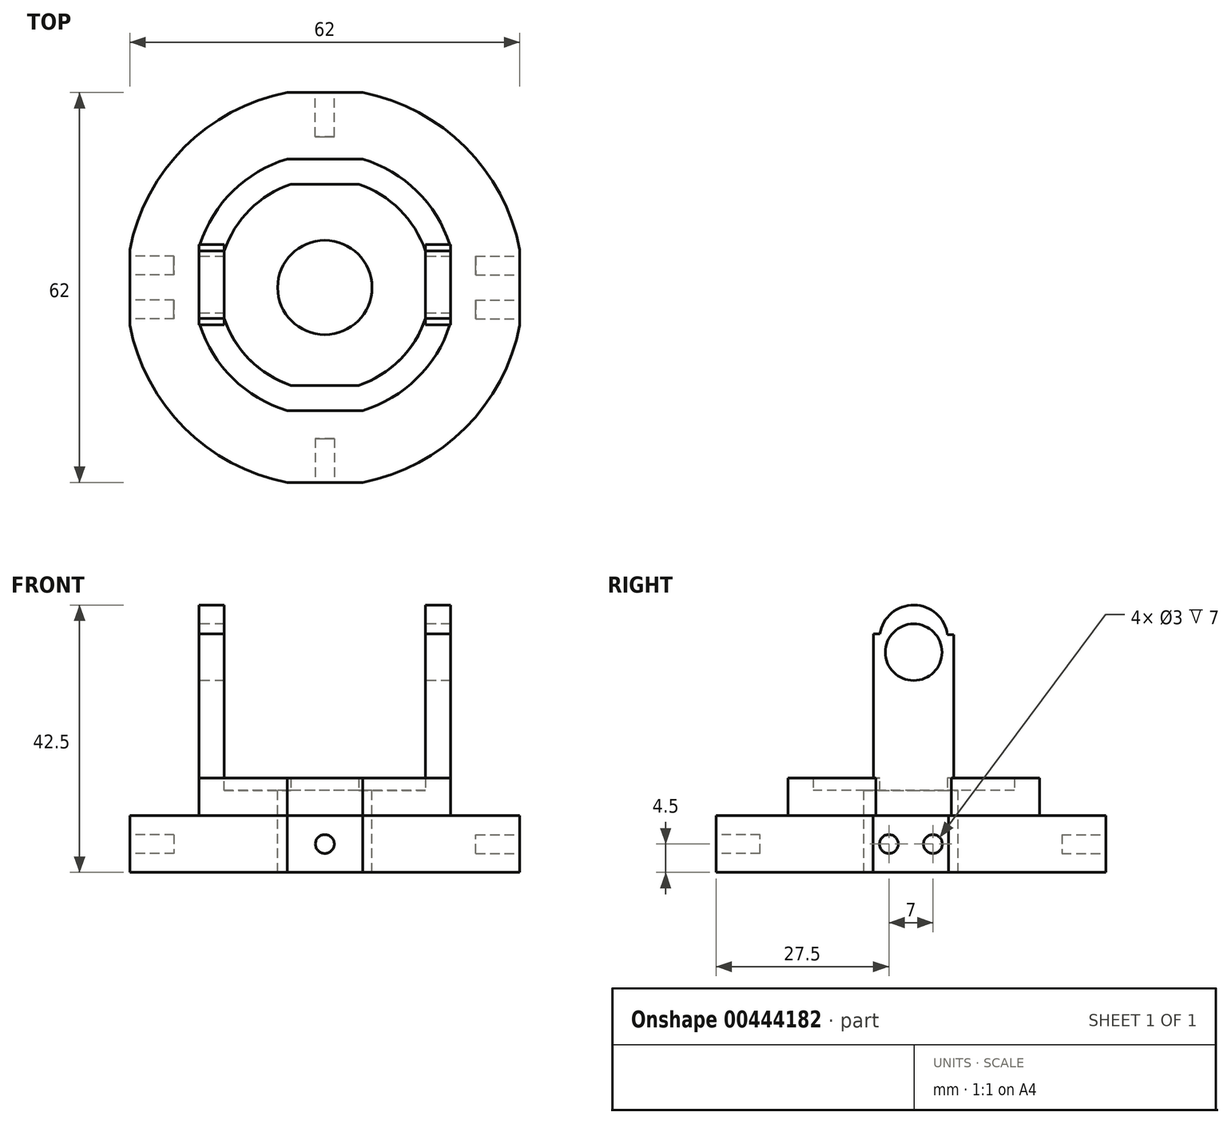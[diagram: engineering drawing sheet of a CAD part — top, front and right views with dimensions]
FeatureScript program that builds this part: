
annotation { "Feature Type Name" : "Feature", "Feature Type Description" : "" }
export const myFeature = defineFeature(function(context is Context, id is Id, definition is map)
    precondition{}
    {
        {
            var Q0;
            Q0=qCreatedBy(makeId("Top.planeOp"),FACE);
            var sketch = newSketch(context, id + "F0", { "sketchPlane" : qUnion([Q0])});
            skLineSegment(sketch, "E0", {"start": v(0, 20.44) * mm, "end": v(6, 20.44) * mm});
            skLineSegment(sketch, "E1", {"start": v(0, 20.44) * mm, "end": v(-6, 20.44) * mm});
            skLineSegment(sketch, "E2", {"start": v(20, 6.44) * mm, "end": v(20, -5.56) * mm});
            skLineSegment(sketch, "E3", {"start": v(0, -19.56) * mm, "end": v(6, -19.56) * mm});
            skLineSegment(sketch, "E4", {"start": v(0, -19.56) * mm, "end": v(-6, -19.56) * mm});
            skLineSegment(sketch, "E5", {"start": v(-20, 0.44) * mm, "end": v(-20, 6.44) * mm});
            skLineSegment(sketch, "E6", {"start": v(-20, 0.44) * mm, "end": v(-20, -5.56) * mm});
            skArc(sketch, "E7", {"start": v(-6, 20.44) * mm, "mid": v(-14.76, 15.2) * mm, "end": v(-20, 6.44) * mm});
            skArc(sketch, "E8.trimOffspring", {"start": v(20, 6.44) * mm, "mid": v(14.76, 15.2) * mm, "end": v(6, 20.44) * mm});
            skArc(sketch, "E9.trimOffspring", {"start": v(-20, -5.56) * mm, "mid": v(-14.76, -14.33) * mm, "end": v(-6, -19.56) * mm});
            skArc(sketch, "E10.trimOffspring", {"start": v(6, -19.56) * mm, "mid": v(14.76, -14.33) * mm, "end": v(20, -5.56) * mm});
            skSolve(sketch);
        }
        {
            var Q0;
            Q0=makeQuery(id+"F0.imprint","IMPRINT",FACE,{"disambiguationData":[TD([[makeQuery(id+"F0.imprint","IMPRINT",EDGE,{"derivedFrom":sQuery(id+"F0.wireOp",EDGE,"E0")}),-1.0]])]});
            extrude(context, id + "F1", {"entities" : qUnion([Q0]), "depth" : 6 * mm});
        }
        {
            var Q0;
            Q0=makeQuery(id+"F1.opExtrude","CAP_FACE",FACE,{"disambiguationData":[OSD([sQuery(id+"F0.wireOp",EDGE,"E0"),sQuery(id+"F0.wireOp",EDGE,"E1"),sQuery(id+"F0.wireOp",EDGE,"E2"),sQuery(id+"F0.wireOp",EDGE,"E3"),sQuery(id+"F0.wireOp",EDGE,"E4"),sQuery(id+"F0.wireOp",EDGE,"E5"),sQuery(id+"F0.wireOp",EDGE,"E6"),sQuery(id+"F0.wireOp",EDGE,"E7"),sQuery(id+"F0.wireOp",EDGE,"E8.trimOffspring"),sQuery(id+"F0.wireOp",EDGE,"E9.trimOffspring"),sQuery(id+"F0.wireOp",EDGE,"E10.trimOffspring")])],"isStart":false});
            shell(context, id + "F2", {"entities" : qUnion([Q0]), "thickness" : 4 * mm});
        }
        {
            var Q0;
            Q0=makeQuery(id+"F2.opShell","OFFSET_FACE",FACE,{"disambiguationData":[OSD([sQuery(id+"F0.wireOp",EDGE,"E0"),sQuery(id+"F0.wireOp",EDGE,"E1"),sQuery(id+"F0.wireOp",EDGE,"E2"),sQuery(id+"F0.wireOp",EDGE,"E3"),sQuery(id+"F0.wireOp",EDGE,"E4"),sQuery(id+"F0.wireOp",EDGE,"E5"),sQuery(id+"F0.wireOp",EDGE,"E6"),sQuery(id+"F0.wireOp",EDGE,"E7"),sQuery(id+"F0.wireOp",EDGE,"E8.trimOffspring"),sQuery(id+"F0.wireOp",EDGE,"E9.trimOffspring"),sQuery(id+"F0.wireOp",EDGE,"E10.trimOffspring")])]});
            extrude(context, id + "F3", {"entities" : qUnion([Q0]), "operationType" : NewBodyOperationType.REMOVE, "oppositeDirection" : true, "depth" : 25.4 * mm});
        }
        {
            var Q0;
            {var subQ0=sQuery(id+"F0.wireOp",EDGE,"E2");Q0=makeQuery(id+"F3.boolean.opBoolean","MERGE",FACE,{"derivedFrom":[makeQuery(id+"F2.opShell","OFFSET_FACE",FACE,{"disambiguationData":[OSD([subQ0])]}),makeQuery(id+"F3.opExtrude","SWEPT_FACE",FACE,{"disambiguationData":[OSD([subQ0])]})]});}
            var sketch = newSketch(context, id + "F4", { "sketchPlane" : qUnion([Q0])});
            skLineSegment(sketch, "E11.bottom", {"start": v(4.94, 6) * mm, "end": v(-5.82, 6) * mm});
            skLineSegment(sketch, "E11.top", {"start": v(4.94, 33.5) * mm, "end": v(-5.82, 33.5) * mm});
            skLineSegment(sketch, "E11.left", {"start": v(4.94, 6) * mm, "end": v(4.94, 33.5) * mm});
            skLineSegment(sketch, "E11.right", {"start": v(-5.82, 6) * mm, "end": v(-5.82, 33.5) * mm});
            skSolve(sketch);
        }
        {
            var Q0;
            Q0=makeQuery(id+"F4.imprint","IMPRINT",FACE,{"disambiguationData":[TD([[makeQuery(id+"F4.imprint","IMPRINT",EDGE,{"derivedFrom":sQuery(id+"F4.wireOp",EDGE,"E11.bottom")}),1.0]])]});
            extrude(context, id + "F5", {"entities" : qUnion([Q0]), "operationType" : NewBodyOperationType.ADD, "oppositeDirection" : true, "depth" : 4 * mm});
        }
        {
            var Q0;
            {var subQ0=sQuery(id+"F0.wireOp",EDGE,"E6");var subQ1=sQuery(id+"F0.wireOp",EDGE,"E5");Q0=makeQuery(id+"F3.boolean.opBoolean","MERGE",FACE,{"derivedFrom":[makeQuery(id+"F2.opShell","OFFSET_FACE",FACE,{"disambiguationData":[OSD([subQ1,subQ0])]}),makeQuery(id+"F3.opExtrude","SWEPT_FACE",FACE,{"disambiguationData":[OSD([subQ1,subQ0])]})]});}
            var sketch = newSketch(context, id + "F6", { "sketchPlane" : qUnion([Q0])});
            skLineSegment(sketch, "E12.bottom", {"start": v(5.82, 6) * mm, "end": v(-4.94, 6) * mm});
            skLineSegment(sketch, "E12.top", {"start": v(5.82, 33.5) * mm, "end": v(-4.94, 33.5) * mm});
            skLineSegment(sketch, "E12.left", {"start": v(5.82, 6) * mm, "end": v(5.82, 33.5) * mm});
            skLineSegment(sketch, "E12.right", {"start": v(-4.94, 6) * mm, "end": v(-4.94, 33.5) * mm});
            skSolve(sketch);
        }
        {
            var Q0;
            Q0=makeQuery(id+"F6.imprint","IMPRINT",FACE,{"disambiguationData":[TD([[makeQuery(id+"F6.imprint","IMPRINT",EDGE,{"derivedFrom":sQuery(id+"F6.wireOp",EDGE,"E12.bottom")}),1.0]])]});
            extrude(context, id + "F7", {"entities" : qUnion([Q0]), "operationType" : NewBodyOperationType.ADD, "oppositeDirection" : true, "depth" : 4 * mm});
        }
        {
            var Q0;
            Q0=makeQuery(id+"F7.boolean.opBoolean","MERGE",FACE,{"derivedFrom":[makeQuery(id+"F1.opExtrude","SWEPT_FACE",FACE,{"disambiguationData":[OSD([sQuery(id+"F0.wireOp",EDGE,"E5"),sQuery(id+"F0.wireOp",EDGE,"E6")])]}),makeQuery(id+"F7.opExtrude","CAP_FACE",FACE,{"disambiguationData":[OSD([sQuery(id+"F6.wireOp",EDGE,"E12.bottom"),sQuery(id+"F6.wireOp",EDGE,"E12.top"),sQuery(id+"F6.wireOp",EDGE,"E12.left"),sQuery(id+"F6.wireOp",EDGE,"E12.right")])],"isStart":false})]});
            var sketch = newSketch(context, id + "F8", { "sketchPlane" : qUnion([Q0])});
            skCircle(sketch, "E13", {"center": v(-0.44, 26) * mm, "radius": 4.5 * mm});
            skPoint(sketch, "E14.orphan", {"position": v(-0.44, 33.5) * mm});
            skLineSegment(sketch, "E15", {"start": v(-0.44, 33.5) * mm, "end": v(-0.44, 28.06) * mm, "construction": true});
            skArc(sketch, "E16", {"start": v(3.9, 24.77) * mm, "mid": v(-0.44, 33.5) * mm, "end": v(-4.76, 24.77) * mm});
            skSolve(sketch);
        }
        {
            var Q0;
            {var subQ0=sQuery(id+"F8.wireOp",EDGE,"E16");var subQ1=makeQuery(id+"F7.opExtrude","CAP_EDGE",EDGE,{"disambiguationData":[OSD([sQuery(id+"F6.wireOp",EDGE,"E12.top")])],"isStart":false});var subQ2=makeQuery(id+"F8.imprint","INTERSECT",VERTEX,{"derivedFrom":[subQ1,subQ0]});Q0=makeQuery(id+"F8.imprint","IMPRINT",FACE,{"disambiguationData":[TD([[makeQuery(id+"F8.imprint","IMPRINT",EDGE,{"disambiguationData":[TD([[subQ2,-1.0]])],"derivedFrom":subQ0}),-1.0]])]});}
            extrude(context, id + "F9", {"entities" : qUnion([Q0]), "operationType" : NewBodyOperationType.REMOVE, "oppositeDirection" : true, "depth" : 50 * mm});
        }
        {
            var Q0;
            {var subQ0=sQuery(id+"F8.wireOp",EDGE,"E16");var subQ1=makeQuery(id+"F7.opExtrude","CAP_EDGE",EDGE,{"disambiguationData":[OSD([sQuery(id+"F6.wireOp",EDGE,"E12.right")])],"isStart":false});var subQ2=makeQuery(id+"F8.imprint","INTERSECT",VERTEX,{"disambiguationData":[OD(1.0)],"derivedFrom":[subQ1,subQ0]});Q0=makeQuery(id+"F8.imprint","IMPRINT",FACE,{"disambiguationData":[TD([[makeQuery(id+"F8.imprint","IMPRINT",EDGE,{"disambiguationData":[TD([[subQ2,-1.0]])],"derivedFrom":subQ0}),-1.0]])]});}
            extrude(context, id + "F10", {"entities" : qUnion([Q0]), "operationType" : NewBodyOperationType.REMOVE, "oppositeDirection" : true, "depth" : 50 * mm});
        }
        {
            var Q0;
            {var subQ0=sQuery(id+"F8.wireOp",EDGE,"E16");var subQ1=sQuery(id+"F8.wireOp",EDGE,"E13");var subQ2=makeQuery(id+"F8.imprint","INTERSECT",VERTEX,{"disambiguationData":[OD(0.0)],"derivedFrom":[subQ1,subQ0]});Q0=makeQuery(id+"F8.imprint","IMPRINT",FACE,{"disambiguationData":[TD([[makeQuery(id+"F8.imprint","IMPRINT",EDGE,{"disambiguationData":[TD([[subQ2,1.0]])],"derivedFrom":subQ1}),1.0]])]});}
            extrude(context, id + "F11", {"entities" : qUnion([Q0]), "operationType" : NewBodyOperationType.REMOVE, "oppositeDirection" : true, "depth" : 50 * mm});
        }
        {
            var Q0;
            Q0=makeQuery(id+"F7.opExtrude","SWEPT_FACE",FACE,{"disambiguationData":[OSD([sQuery(id+"F6.wireOp",EDGE,"E12.left")])]});
            extrude(context, id + "F12", {"entities" : qUnion([Q0]), "operationType" : NewBodyOperationType.ADD, "depth" : 1 * mm});
        }
        {
            var Q0;
            Q0=makeQuery(id+"F7.opExtrude","SWEPT_FACE",FACE,{"disambiguationData":[OSD([sQuery(id+"F6.wireOp",EDGE,"E12.right")])]});
            extrude(context, id + "F13", {"entities" : qUnion([Q0]), "operationType" : NewBodyOperationType.ADD, "depth" : 1 * mm});
        }
        {
            var Q0;
            Q0=makeQuery(id+"F5.opExtrude","SWEPT_FACE",FACE,{"disambiguationData":[OSD([sQuery(id+"F4.wireOp",EDGE,"E11.right")])]});
            extrude(context, id + "F14", {"entities" : qUnion([Q0]), "operationType" : NewBodyOperationType.ADD, "depth" : 1 * mm});
        }
        {
            var Q0;
            Q0=makeQuery(id+"F5.opExtrude","SWEPT_FACE",FACE,{"disambiguationData":[OSD([sQuery(id+"F4.wireOp",EDGE,"E11.left")])]});
            extrude(context, id + "F15", {"entities" : qUnion([Q0]), "operationType" : NewBodyOperationType.ADD, "depth" : 1 * mm});
        }
        {
            var Q0;
            Q0=qCreatedBy(makeId("Top.planeOp"),FACE);
            var sketch = newSketch(context, id + "F16", { "sketchPlane" : qUnion([Q0])});
            skLineSegment(sketch, "E17", {"start": v(-16.05, 0) * mm, "end": v(16.02, 0) * mm, "construction": true});
            skSolve(sketch);
        }
        {
            var Q0;
            Q0=makeQuery(id+"F1.opExtrude","CAP_FACE",FACE,{"disambiguationData":[OSD([sQuery(id+"F0.wireOp",EDGE,"E0"),sQuery(id+"F0.wireOp",EDGE,"E1"),sQuery(id+"F0.wireOp",EDGE,"E2"),sQuery(id+"F0.wireOp",EDGE,"E3"),sQuery(id+"F0.wireOp",EDGE,"E4"),sQuery(id+"F0.wireOp",EDGE,"E5"),sQuery(id+"F0.wireOp",EDGE,"E6"),sQuery(id+"F0.wireOp",EDGE,"E7"),sQuery(id+"F0.wireOp",EDGE,"E8.trimOffspring"),sQuery(id+"F0.wireOp",EDGE,"E9.trimOffspring"),sQuery(id+"F0.wireOp",EDGE,"E10.trimOffspring")])],"isStart":true});
            var sketch = newSketch(context, id + "F17", { "sketchPlane" : qUnion([Q0])});
            skLineSegment(sketch, "E18.bottom", {"start": v(-16, -0.44) * mm, "end": v(0, -0.44) * mm});
            skLineSegment(sketch, "E18.top", {"start": v(-16, 15.56) * mm, "end": v(0, 15.56) * mm});
            skLineSegment(sketch, "E18.left", {"start": v(-16, -0.44) * mm, "end": v(-16, 15.56) * mm});
            skLineSegment(sketch, "E18.right", {"start": v(0, -0.44) * mm, "end": v(0, 15.56) * mm});
            skLineSegment(sketch, "E19.bottom", {"start": v(16, -0.44) * mm, "end": v(0, -0.44) * mm});
            skLineSegment(sketch, "E19.top", {"start": v(16, 15.56) * mm, "end": v(0, 15.56) * mm});
            skLineSegment(sketch, "E19.left", {"start": v(16, -0.44) * mm, "end": v(16, 15.56) * mm});
            skLineSegment(sketch, "E20.top", {"start": v(-16, -16.44) * mm, "end": v(0, -16.44) * mm});
            skLineSegment(sketch, "E20.left", {"start": v(-16, -0.44) * mm, "end": v(-16, -16.44) * mm});
            skLineSegment(sketch, "E20.right", {"start": v(0, -0.44) * mm, "end": v(0, -16.44) * mm});
            skLineSegment(sketch, "E21.top", {"start": v(16, -16.44) * mm, "end": v(0, -16.44) * mm});
            skLineSegment(sketch, "E21.left", {"start": v(16, -0.44) * mm, "end": v(16, -16.44) * mm});
            skCircle(sketch, "E22", {"center": v(0, -0.44) * mm, "radius": 16.88 * mm});
            skSolve(sketch);
        }
        {
            var Q0;
            {var subQ0=sQuery(id+"F17.wireOp",EDGE,"E18.right");Q0=makeQuery(id+"F17.imprint","IMPRINT",FACE,{"disambiguationData":[TD([[makeQuery(id+"F17.imprint","IMPRINT",EDGE,{"derivedFrom":subQ0}),-1.0]])]});}
            var Q1;
            {var subQ4=sQuery(id+"F17.wireOp",EDGE,"E18.right");Q1=makeQuery(id+"F17.imprint","IMPRINT",FACE,{"disambiguationData":[TD([[makeQuery(id+"F17.imprint","IMPRINT",EDGE,{"derivedFrom":subQ4}),1.0]])]});}
            var Q2;
            {var subQ6=sQuery(id+"F17.wireOp",EDGE,"E18.bottom");Q2=makeQuery(id+"F17.imprint","IMPRINT",FACE,{"disambiguationData":[TD([[makeQuery(id+"F17.imprint","IMPRINT",EDGE,{"derivedFrom":subQ6}),-1.0]])]});}
            var Q3;
            {var subQ4=sQuery(id+"F17.wireOp",EDGE,"E19.bottom");Q3=makeQuery(id+"F17.imprint","IMPRINT",FACE,{"disambiguationData":[TD([[makeQuery(id+"F17.imprint","IMPRINT",EDGE,{"derivedFrom":subQ4}),1.0]])]});}
            extrude(context, id + "F18", {"entities" : qUnion([Q0, Q1, Q2, Q3]), "operationType" : NewBodyOperationType.ADD, "oppositeDirection" : true, "depth" : 4 * mm});
        }
        {
            var Q0;
            Q0=makeQuery(id+"F18.boolean.opBoolean","MERGE",FACE,{"derivedFrom":[makeQuery(id+"F1.opExtrude","CAP_FACE",FACE,{"disambiguationData":[OSD([sQuery(id+"F0.wireOp",EDGE,"E0"),sQuery(id+"F0.wireOp",EDGE,"E1"),sQuery(id+"F0.wireOp",EDGE,"E2"),sQuery(id+"F0.wireOp",EDGE,"E3"),sQuery(id+"F0.wireOp",EDGE,"E4"),sQuery(id+"F0.wireOp",EDGE,"E5"),sQuery(id+"F0.wireOp",EDGE,"E6"),sQuery(id+"F0.wireOp",EDGE,"E7"),sQuery(id+"F0.wireOp",EDGE,"E8.trimOffspring"),sQuery(id+"F0.wireOp",EDGE,"E9.trimOffspring"),sQuery(id+"F0.wireOp",EDGE,"E10.trimOffspring")])],"isStart":true}),makeQuery(id+"F18.opExtrude","CAP_FACE",FACE,{"disambiguationData":[OSD([sQuery(id+"F17.wireOp",EDGE,"E18.top"),sQuery(id+"F17.wireOp",EDGE,"E18.left"),sQuery(id+"F17.wireOp",EDGE,"E19.top"),sQuery(id+"F17.wireOp",EDGE,"E19.left"),sQuery(id+"F17.wireOp",EDGE,"E20.top"),sQuery(id+"F17.wireOp",EDGE,"E20.left"),sQuery(id+"F17.wireOp",EDGE,"E21.top"),sQuery(id+"F17.wireOp",EDGE,"E21.left"),sQuery(id+"F17.wireOp",EDGE,"E22")])],"isStart":true})]});
            var sketch = newSketch(context, id + "F19", { "sketchPlane" : qUnion([Q0])});
            skPoint(sketch, "E23.start.orphan", {"position": v(0, 0) * mm});
            skLineSegment(sketch, "E24.top", {"start": v(0, 31) * mm, "end": v(6, 31) * mm});
            skLineSegment(sketch, "E25.bottom", {"start": v(6, 31) * mm, "end": v(-6, 31) * mm});
            skLineSegment(sketch, "E25.top", {"start": v(6, -31) * mm, "end": v(-6, -31) * mm});
            skLineSegment(sketch, "E26.right", {"start": v(31, 0) * mm, "end": v(31, 6) * mm});
            skLineSegment(sketch, "E27.left", {"start": v(31, 6) * mm, "end": v(31, -6) * mm});
            skLineSegment(sketch, "E27.right", {"start": v(-31, 6) * mm, "end": v(-31, -6) * mm});
            skArc(sketch, "E28", {"start": v(6, -31) * mm, "mid": v(22.33, -22.33) * mm, "end": v(31, -6) * mm});
            skArc(sketch, "E29.trimOffspring", {"start": v(31, 6) * mm, "mid": v(22.33, 22.33) * mm, "end": v(6, 31) * mm});
            skArc(sketch, "E30.trimOffspring", {"start": v(-31, -6) * mm, "mid": v(-22.33, -22.33) * mm, "end": v(-6, -31) * mm});
            skArc(sketch, "E31.trimOffspring", {"start": v(-6, 31) * mm, "mid": v(-22.33, 22.33) * mm, "end": v(-31, 6) * mm});
            skPoint(sketch, "E24.bottom.end.orphan", {"position": v(6, 0) * mm});
            skPoint(sketch, "E26.top.start.orphan", {"position": v(0, 6) * mm});
            skSolve(sketch);
        }
        {
            var Q0;
            Q0 = qSketchRegion(id + "F19", true);
            extrude(context, id + "F20", {"entities" : qUnion([Q0]), "operationType" : NewBodyOperationType.ADD, "depth" : 9 * mm});
        }
        {
            var Q0;
            Q0=makeQuery(id+"F20.opExtrude","SWEPT_FACE",FACE,{"disambiguationData":[OSD([sQuery(id+"F19.wireOp",EDGE,"E25.bottom")])]});
            var sketch = newSketch(context, id + "F21", { "sketchPlane" : qUnion([Q0])});
            skLineSegment(sketch, "E32", {"start": v(0, 0) * mm, "end": v(0, -4.5) * mm, "construction": true});
            skCircle(sketch, "E33", {"center": v(0, -4.5) * mm, "radius": 1.5 * mm});
            skSolve(sketch);
        }
        {
            var Q0;
            Q0=makeQuery(id+"F21.imprint","IMPRINT",FACE,{"disambiguationData":[TD([[makeQuery(id+"F21.imprint","IMPRINT",EDGE,{"derivedFrom":sQuery(id+"F21.wireOp",EDGE,"E33")}),1.0]])]});
            extrude(context, id + "F22", {"entities" : qUnion([Q0]), "operationType" : NewBodyOperationType.REMOVE, "oppositeDirection" : true, "depth" : 7 * mm});
        }
        {
            var Q0;
            Q0=makeQuery(id+"F20.opExtrude","SWEPT_FACE",FACE,{"disambiguationData":[OSD([sQuery(id+"F19.wireOp",EDGE,"E25.top")])]});
            var sketch = newSketch(context, id + "F23", { "sketchPlane" : qUnion([Q0])});
            skLineSegment(sketch, "E34", {"start": v(0, 0) * mm, "end": v(0, -4.5) * mm, "construction": true});
            skCircle(sketch, "E35", {"center": v(0, -4.5) * mm, "radius": 1.5 * mm});
            skSolve(sketch);
        }
        {
            var Q0;
            Q0=makeQuery(id+"F23.imprint","IMPRINT",FACE,{"disambiguationData":[TD([[makeQuery(id+"F23.imprint","IMPRINT",EDGE,{"derivedFrom":sQuery(id+"F23.wireOp",EDGE,"E35")}),1.0]])]});
            extrude(context, id + "F24", {"entities" : qUnion([Q0]), "operationType" : NewBodyOperationType.REMOVE, "oppositeDirection" : true, "depth" : 7 * mm});
        }
        {
            var Q0;
            Q0=makeQuery(id+"F20.opExtrude","SWEPT_FACE",FACE,{"disambiguationData":[OSD([sQuery(id+"F19.wireOp",EDGE,"E27.left")])]});
            var sketch = newSketch(context, id + "F25", { "sketchPlane" : qUnion([Q0])});
            skLineSegment(sketch, "E36", {"start": v(0, 0) * mm, "end": v(0, -9) * mm, "construction": true});
            skLineSegment(sketch, "E37", {"start": v(0, -4.5) * mm, "end": v(3.5, -4.5) * mm, "construction": true});
            skLineSegment(sketch, "E38", {"start": v(0, -4.5) * mm, "end": v(-3.5, -4.5) * mm, "construction": true});
            skCircle(sketch, "E39", {"center": v(-3.5, -4.5) * mm, "radius": 1.5 * mm});
            skCircle(sketch, "E40", {"center": v(3.5, -4.5) * mm, "radius": 1.5 * mm});
            skSolve(sketch);
        }
        {
            var Q0;
            Q0=makeQuery(id+"F25.imprint","IMPRINT",FACE,{"disambiguationData":[TD([[makeQuery(id+"F25.imprint","IMPRINT",EDGE,{"derivedFrom":sQuery(id+"F25.wireOp",EDGE,"E39")}),1.0]])]});
            var Q1;
            Q1=makeQuery(id+"F25.imprint","IMPRINT",FACE,{"disambiguationData":[TD([[makeQuery(id+"F25.imprint","IMPRINT",EDGE,{"derivedFrom":sQuery(id+"F25.wireOp",EDGE,"E40")}),1.0]])]});
            extrude(context, id + "F26", {"entities" : qUnion([Q0, Q1]), "operationType" : NewBodyOperationType.REMOVE, "oppositeDirection" : true, "depth" : 7 * mm});
        }
        {
            var Q0;
            Q0=makeQuery(id+"F20.opExtrude","SWEPT_FACE",FACE,{"disambiguationData":[OSD([sQuery(id+"F19.wireOp",EDGE,"E27.right")])]});
            var sketch = newSketch(context, id + "F27", { "sketchPlane" : qUnion([Q0])});
            skLineSegment(sketch, "E41", {"start": v(0, 0) * mm, "end": v(0, -9) * mm, "construction": true});
            skLineSegment(sketch, "E42", {"start": v(0, -4.5) * mm, "end": v(3.5, -4.5) * mm, "construction": true});
            skLineSegment(sketch, "E43", {"start": v(0, -4.5) * mm, "end": v(-3.5, -4.5) * mm, "construction": true});
            skCircle(sketch, "E44", {"center": v(3.5, -4.5) * mm, "radius": 1.5 * mm});
            skCircle(sketch, "E45", {"center": v(-3.5, -4.5) * mm, "radius": 1.5 * mm});
            skSolve(sketch);
        }
        {
            var Q0;
            Q0=makeQuery(id+"F27.imprint","IMPRINT",FACE,{"disambiguationData":[TD([[makeQuery(id+"F27.imprint","IMPRINT",EDGE,{"derivedFrom":sQuery(id+"F27.wireOp",EDGE,"E45")}),1.0]])]});
            var Q1;
            Q1=makeQuery(id+"F27.imprint","IMPRINT",FACE,{"disambiguationData":[TD([[makeQuery(id+"F27.imprint","IMPRINT",EDGE,{"derivedFrom":sQuery(id+"F27.wireOp",EDGE,"E44")}),1.0]])]});
            extrude(context, id + "F28", {"entities" : qUnion([Q0, Q1]), "operationType" : NewBodyOperationType.REMOVE, "oppositeDirection" : true, "depth" : 7 * mm});
        }
        {
            var Q0;
            Q0=makeQuery(id+"F18.opExtrude","CAP_FACE",FACE,{"disambiguationData":[OSD([sQuery(id+"F17.wireOp",EDGE,"E18.top"),sQuery(id+"F17.wireOp",EDGE,"E18.left"),sQuery(id+"F17.wireOp",EDGE,"E19.top"),sQuery(id+"F17.wireOp",EDGE,"E19.left"),sQuery(id+"F17.wireOp",EDGE,"E20.top"),sQuery(id+"F17.wireOp",EDGE,"E20.left"),sQuery(id+"F17.wireOp",EDGE,"E21.top"),sQuery(id+"F17.wireOp",EDGE,"E21.left"),sQuery(id+"F17.wireOp",EDGE,"E22")])],"isStart":false});
            var sketch = newSketch(context, id + "F29", { "sketchPlane" : qUnion([Q0])});
            skCircle(sketch, "E46", {"center": v(0, 0) * mm, "radius": 7.5 * mm});
            skSolve(sketch);
        }
        {
            var Q0;
            Q0=makeQuery(id+"F29.imprint","IMPRINT",FACE,{"disambiguationData":[TD([[makeQuery(id+"F29.imprint","IMPRINT",EDGE,{"derivedFrom":sQuery(id+"F29.wireOp",EDGE,"E46")}),1.0]])]});
            extrude(context, id + "F30", {"entities" : qUnion([Q0]), "operationType" : NewBodyOperationType.REMOVE, "oppositeDirection" : true, "depth" : 25.4 * mm});
        }
    });
